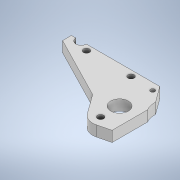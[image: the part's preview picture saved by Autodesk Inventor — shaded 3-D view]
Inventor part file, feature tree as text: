
AUTODESK INVENTOR PART (.ipt)
format: ipt  version: 2022 (Build 260153000, 153)  size: 133,120 bytes
history: native  units: mm
features: extrude x1, fillet x1, sketch x1
ambient origin geometry x8: Origin, YZ Plane, XZ Plane, XY Plane, X Axis, Y Axis, Z Axis, Center Point
bodies: Solid1 (feature_tree)
feature tree (3):
  extrude  "Extrusion1"  Depth=7.5mm
  fillet  "Fillet1"  Radius=12.0mm
  sketch  "Sketch1"  dims[d2=50.0mm d6=11.0mm d7=12.0mm d8=20.0mm d15=3.5mm d16=17.0mm d17=10.0mm d23=2.5mm d26=3.5mm d28=2.5mm d30=3.0mm d31=6.0mm d32=0.0mm d33=7.5mm]
